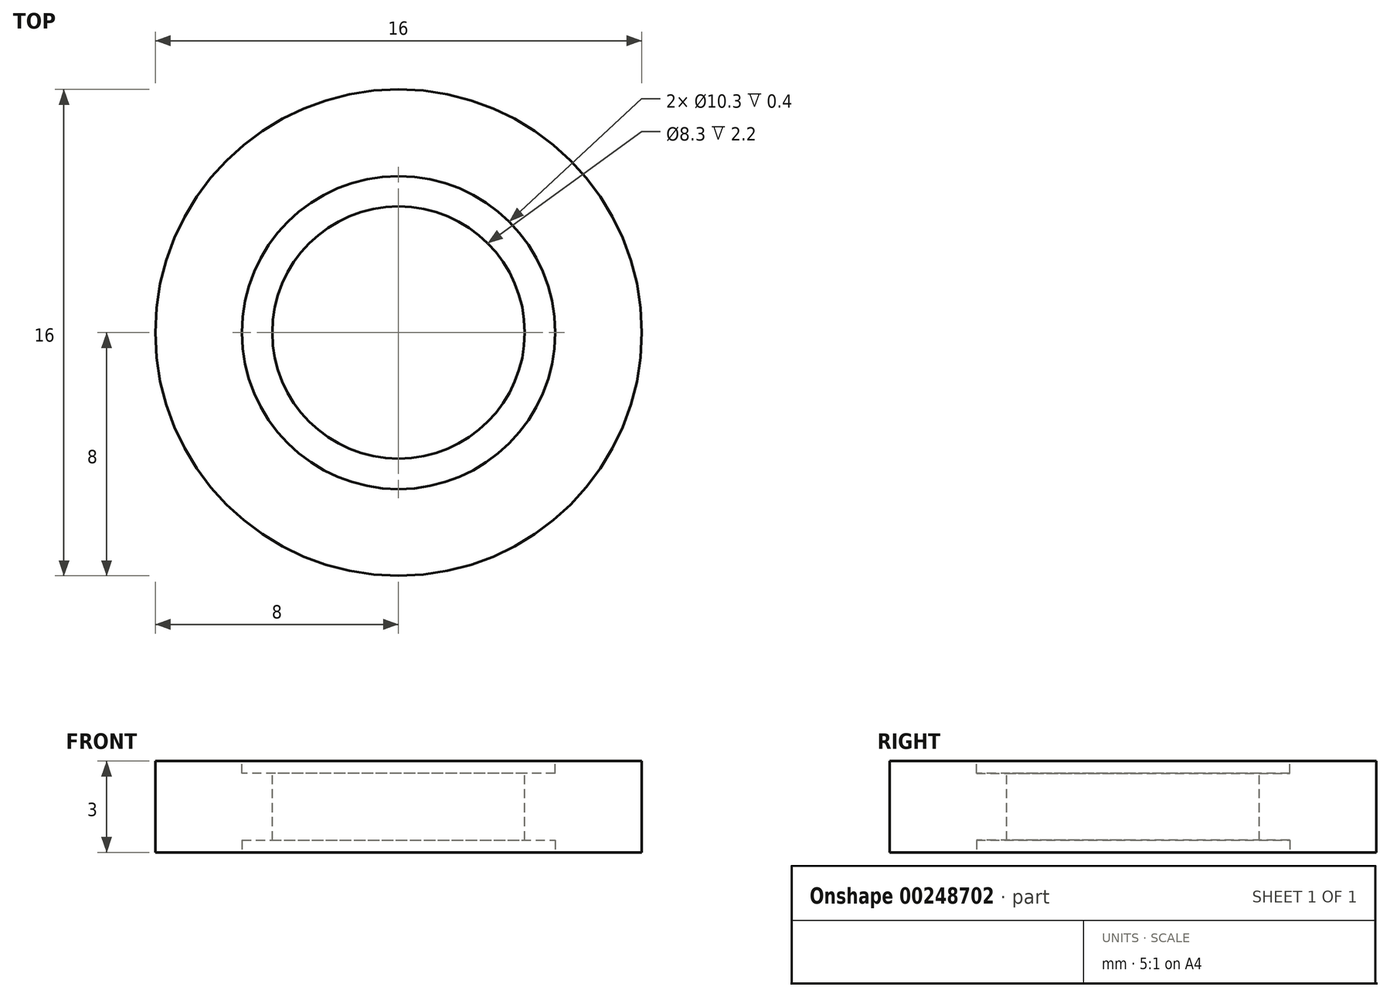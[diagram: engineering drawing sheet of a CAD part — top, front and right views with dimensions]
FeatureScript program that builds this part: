
annotation { "Feature Type Name" : "Feature", "Feature Type Description" : "" }
export const myFeature = defineFeature(function(context is Context, id is Id, definition is map)
    precondition{}
    {
        {
            var Q0;
            Q0=qCreatedBy(makeId("Top.planeOp"),FACE);
            var sketch = newSketch(context, id + "F0", { "sketchPlane" : qUnion([Q0])});
            skCircle(sketch, "E0", {"center": v(0, 0) * mm, "radius": 8 * mm});
            skSolve(sketch);
        }
        {
            var Q0;
            Q0 = qSketchRegion(id + "F0", true);
            extrude(context, id + "F1", {"entities" : qUnion([Q0]), "depth" : 3 * mm});
        }
        {
            var Q0;
            Q0=makeQuery(id+"F1.opExtrude","CAP_FACE",FACE,{"disambiguationData":[OSD([sQuery(id+"F0.wireOp",EDGE,"E0")])],"isStart":false});
            var sketch = newSketch(context, id + "F2", { "sketchPlane" : qUnion([Q0])});
            skCircle(sketch, "E1", {"center": v(0, 0) * mm, "radius": 4.15 * mm});
            skSolve(sketch);
        }
        {
            var Q0;
            Q0 = qSketchRegion(id + "F2", true);
            extrude(context, id + "F3", {"entities" : qUnion([Q0]), "operationType" : NewBodyOperationType.REMOVE, "oppositeDirection" : true, "depth" : 25 * mm});
        }
        {
            var Q0;
            Q0=makeQuery(id+"F1.opExtrude","CAP_FACE",FACE,{"disambiguationData":[OSD([sQuery(id+"F0.wireOp",EDGE,"E0")])],"isStart":false});
            var sketch = newSketch(context, id + "F4", { "sketchPlane" : qUnion([Q0])});
            skCircle(sketch, "E2", {"center": v(0, 0) * mm, "radius": 5.15 * mm});
            skSolve(sketch);
        }
        {
            var Q0;
            Q0 = qSketchRegion(id + "F4", true);
            extrude(context, id + "F5", {"entities" : qUnion([Q0]), "operationType" : NewBodyOperationType.REMOVE, "oppositeDirection" : true, "depth" : 0.4 * mm});
        }
        {
            var Q0;
            Q0=makeQuery(id+"F1.opExtrude","CAP_FACE",FACE,{"disambiguationData":[OSD([sQuery(id+"F0.wireOp",EDGE,"E0")])],"isStart":true});
            var sketch = newSketch(context, id + "F6", { "sketchPlane" : qUnion([Q0])});
            skCircle(sketch, "E3", {"center": v(0, 0) * mm, "radius": 5.15 * mm});
            skSolve(sketch);
        }
        {
            var Q0;
            Q0 = qSketchRegion(id + "F6", true);
            extrude(context, id + "F7", {"entities" : qUnion([Q0]), "operationType" : NewBodyOperationType.REMOVE, "oppositeDirection" : true, "depth" : 0.4 * mm});
        }
    });
